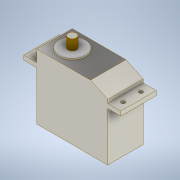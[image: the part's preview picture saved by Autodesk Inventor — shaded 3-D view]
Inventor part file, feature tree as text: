
AUTODESK INVENTOR PART (.ipt)
format: ipt  version: 2020.3 (Build 243373000, 373)  size: 427,008 bytes
history: native  units: mm
features: sketch x8, extrude x7, projected_geometry x6, chamfer x1, pattern_circular x1
ambient origin geometry x8: Origin, YZ Plane, XZ Plane, XY Plane, X Axis, Y Axis, Z Axis, Center Point
bodies: Solid1 (feature_tree)
feature tree (23):
  extrude  "Extrusion1"  Depth=20.1mm
  extrude  "Extrusion2"  Depth=55.0mm
  extrude  "Extrusion3"  TaperAngle=0.0deg  [1 undecoded]
  extrude  "Extrusion4"  Depth=10.0mm TaperAngle=0.0deg
  extrude  "Extrusion5"  Depth=0.7mm TaperAngle=0.0deg
  extrude  "Extrusion6"  Depth=6.0mm TaperAngle=0.0deg
  chamfer  "Chamfer1"  Distance=9.75mm
  extrude  "Extrusion7"  TaperAngle=45.0deg  [1 undecoded]
  pattern_circular  "Circular Pattern1"  Count=80 Angle=360.0deg
  sketch  "Sketch8"  dims[d24=10.0mm d25=0.0mm d26=800.0mm d27=360.0deg]
  sketch  "Sketch1"  dims[d0=40.2mm d1=20.1mm]
  sketch  "Sketch2"  dims[d2=27.7mm d3=0.0mm d4=55.0mm]
  sketch  "Sketch3"  dims[d5=2.5mm d6=0.0mm d8=0.0mm d9=0.0mm]
  projected_geometry  "Projected Loop1"
  sketch  "Sketch4"  dims[d10=36.8mm d11=10.0mm d12=0.0mm]
  sketch  "Sketch5"  dims[d13=15.0mm d14=0.7mm d15=0.0mm]
  sketch  "Sketch6"  dims[d16=4.5mm d17=6.0mm d18=0.0mm d19=9.75mm d20=2.0mm d21=4.363323mm]
  sketch  "Sketch7"  dims[d22=0.1mm d23=45.0deg]
  projected_geometry  "Projected Loop2"
  projected_geometry  "Projected Loop3"
  projected_geometry  "Projected Loop4"
  projected_geometry  "Projected Loop5"
  projected_geometry  "Projected Loop6"
note: 2 required parameter values undecoded (feature->parameter linkage not recoverable at this tier; creation-order binding heuristic only, values carry confidence <= 0.55)
